# Revit family: Legrand_Hotel_UX_TOUCH_Unite_de_Couloir
name_source: partatom
category: Equipement électrique
units: mm (PartAtom-declared; Revit-internal decimal feet)

## family parameters
Configuration du panneau = Deux colonnes, circuits au sein
Cote de connecteur circulaire = Utiliser le diamètre
Couper avec des vides une fois chargée = Non
Hôte = Face
Partagée = Non
Point de calcul de pièce = Non
Type d'élément = Tableau de raccordement

## types (2) — shared parameters
Adressable = Oui
Autres systèmes de bus = autre
Avec affichage LED = Oui
Avec thermostat d'ambiance = Non
Classe de protection (IP) = IP20
Condition Générale d'Utilisation = https://export.legrand.com
Couleur = noir
Elévation par défaut = 1300 mm  [stored 4.26509 ft]
Fabricant = Legrand
Finition de la surface = brillant
Fréquence d'alimentation MIN-MAX (Hz) = 0-0
Hauteur hors tout = 93 mm  [stored 0.305118 ft]
Largeur hors tout = 129 mm  [stored 0.423228 ft]
Matériau = LEGRAND - Plastique noir
Moyen de programmation = Ordinateur
Nombre de touches = 2
Profondeur d'encastrement = 30 mm  [stored 0.0984252 ft]
Profondeur hors tout = 42 mm  [stored 0.137795 ft]
Programmable = Oui
Résistance aux chocs (IK) = IK02
Site web configurateur = https://uxforupscalehotel.legrand.com
Temperature d'utilisation /d'installation MIN-MAX (°C) = 0-40
Temperature de stockage MIN-MAX (°C) = -20-70
Type de montage = encastré
URL = http://www.legrandoc.com

## per-type parameters (varying)
| type | Commande | Consommation en veille (mA) | Description | Modèle |
| Lecteur Badge Externe | Lecteur externe SCS | 12 | Lecteur externe SCS | 048776 |
| Afficheur de Couloir | Indicateur externe SCS | 8 | Indicateur externe SCS | 048775 |

note: [stored X ft] marks values corroborated as IEEE doubles in the binary element streams (Revit-internal decimal feet)
